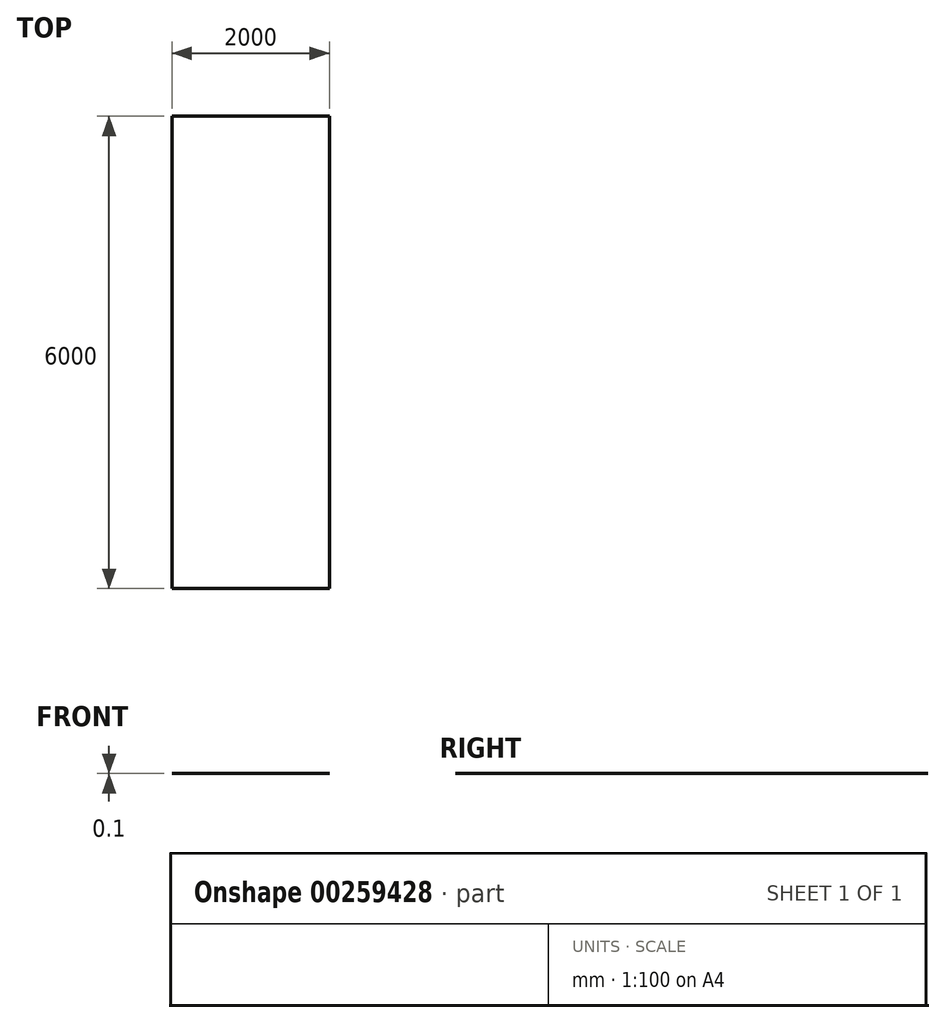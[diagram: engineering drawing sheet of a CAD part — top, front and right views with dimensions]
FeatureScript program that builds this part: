
annotation { "Feature Type Name" : "Feature", "Feature Type Description" : "" }
export const myFeature = defineFeature(function(context is Context, id is Id, definition is map)
    precondition{}
    {
        {
            var Q0;
            Q0=qCreatedBy(makeId("Top.planeOp"),FACE);
            var sketch = newSketch(context, id + "F0", { "sketchPlane" : qUnion([Q0])});
            skLineSegment(sketch, "E0.bottom", {"start": v(0, 0) * mm, "end": v(2000, 0) * mm});
            skLineSegment(sketch, "E0.top", {"start": v(0, 6000) * mm, "end": v(2000, 6000) * mm});
            skLineSegment(sketch, "E0.left", {"start": v(0, 0) * mm, "end": v(0, 6000) * mm});
            skLineSegment(sketch, "E0.right", {"start": v(2000, 0) * mm, "end": v(2000, 6000) * mm});
            skSolve(sketch);
        }
        {
            var Q0;
            Q0 = qSketchRegion(id + "F0", true);
            extrude(context, id + "F1", {"entities" : qUnion([Q0]), "depth" : .1 * mm});
        }
    });
